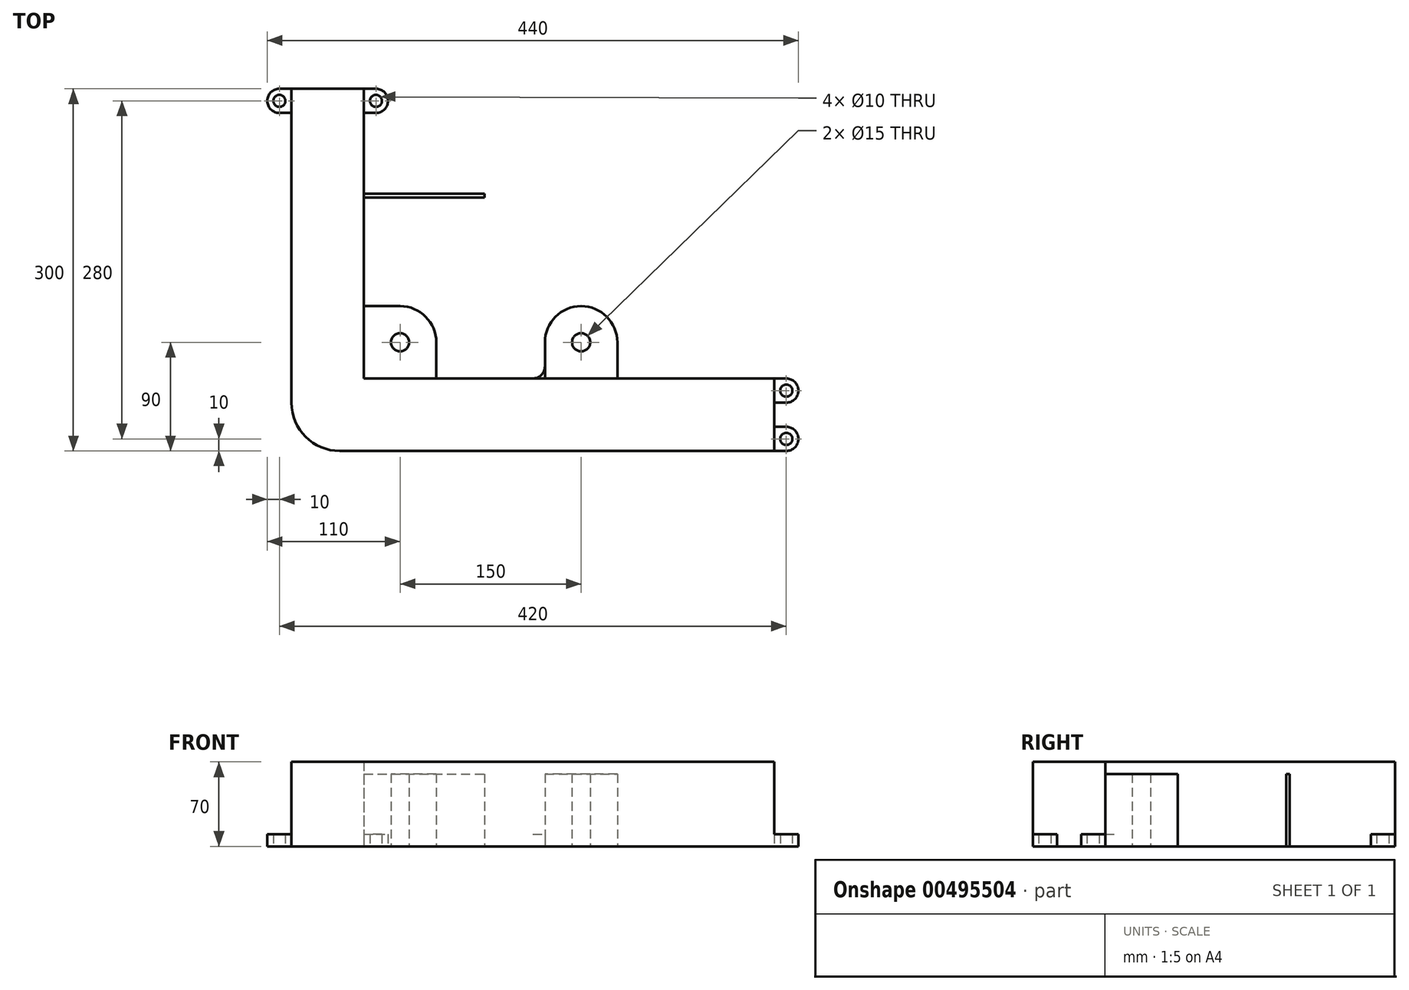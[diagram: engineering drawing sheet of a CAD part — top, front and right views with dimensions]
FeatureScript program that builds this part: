
annotation { "Feature Type Name" : "Feature", "Feature Type Description" : "" }
export const myFeature = defineFeature(function(context is Context, id is Id, definition is map)
    precondition{}
    {
        {
            var Q0;
            Q0=qCreatedBy(makeId("Top.planeOp"),FACE);
            var sketch = newSketch(context, id + "F0", { "sketchPlane" : qUnion([Q0])});
            skLineSegment(sketch, "E0", {"start": v(0, 40) * mm, "end": v(0, 300) * mm});
            skLineSegment(sketch, "E1", {"start": v(400, 60) * mm, "end": v(400, 0) * mm});
            skLineSegment(sketch, "E2", {"start": v(40, 0) * mm, "end": v(400, 0) * mm});
            skLineSegment(sketch, "E3", {"start": v(60, 300) * mm, "end": v(0, 300) * mm});
            skLineSegment(sketch, "E4.top", {"start": v(60, 120) * mm, "end": v(90, 120) * mm});
            skLineSegment(sketch, "E4.right", {"start": v(120, 60) * mm, "end": v(120, 90) * mm});
            skCircle(sketch, "E5", {"center": v(90, 90) * mm, "radius": 7.5 * mm});
            skLineSegment(sketch, "E6", {"start": v(60, 120) * mm, "end": v(60, 300) * mm});
            skLineSegment(sketch, "E7", {"start": v(120, 60) * mm, "end": v(400, 60) * mm});
            skLineSegment(sketch, "E8", {"start": v(60, 120) * mm, "end": v(60, 60) * mm});
            skLineSegment(sketch, "E9", {"start": v(60, 60) * mm, "end": v(120, 60) * mm});
            skLineSegment(sketch, "E10", {"start": v(0, 300) * mm, "end": v(-10, 300) * mm});
            skLineSegment(sketch, "E11", {"start": v(-10, 280) * mm, "end": v(0, 280) * mm});
            skLineSegment(sketch, "E12", {"start": v(60, 300) * mm, "end": v(70, 300) * mm});
            skLineSegment(sketch, "E13", {"start": v(70, 280) * mm, "end": v(60, 280) * mm});
            skLineSegment(sketch, "E14", {"start": v(210, 60) * mm, "end": v(210, 90) * mm});
            skLineSegment(sketch, "E15", {"start": v(270, 90) * mm, "end": v(270, 60) * mm});
            skPoint(sketch, "E16.visualSharp", {"position": v(120, 120) * mm});
            skArc(sketch, "E16.filletArc", {"start": v(120, 90) * mm, "mid": v(111.21, 111.21) * mm, "end": v(90, 120) * mm});
            skLineSegment(sketch, "E17", {"start": v(-10, 300) * mm, "end": v(-10, 280) * mm, "construction": true});
            skLineSegment(sketch, "E18", {"start": v(70, 300) * mm, "end": v(70, 280) * mm, "construction": true});
            skArc(sketch, "E19", {"start": v(-10, 300) * mm, "mid": v(-20, 290) * mm, "end": v(-10, 280) * mm});
            skArc(sketch, "E20", {"start": v(70, 280) * mm, "mid": v(80, 290) * mm, "end": v(70, 300) * mm});
            skCircle(sketch, "E21", {"center": v(-10, 290) * mm, "radius": 5 * mm});
            skArc(sketch, "E22", {"start": v(270, 90) * mm, "mid": v(240, 120) * mm, "end": v(210, 90) * mm});
            skLineSegment(sketch, "E23", {"start": v(210, 90) * mm, "end": v(270, 90) * mm, "construction": true});
            skPoint(sketch, "E24.visualSharp", {"position": v(0, 0) * mm});
            skArc(sketch, "E24.filletArc", {"start": v(0, 40) * mm, "mid": v(11.72, 11.72) * mm, "end": v(40, 0) * mm});
            skLineSegment(sketch, "E25", {"start": v(400, 60) * mm, "end": v(410, 60) * mm});
            skLineSegment(sketch, "E26", {"start": v(410, 60) * mm, "end": v(410, 40) * mm, "construction": true});
            skLineSegment(sketch, "E27", {"start": v(410, 40) * mm, "end": v(400, 40) * mm});
            skLineSegment(sketch, "E28", {"start": v(400, 20) * mm, "end": v(410, 20) * mm});
            skLineSegment(sketch, "E29", {"start": v(410, 20) * mm, "end": v(410, 0) * mm, "construction": true});
            skLineSegment(sketch, "E30", {"start": v(410, 0) * mm, "end": v(400, 0) * mm});
            skCircle(sketch, "E31", {"center": v(70, 290) * mm, "radius": 5 * mm});
            skArc(sketch, "E32", {"start": v(410, 40) * mm, "mid": v(420, 50) * mm, "end": v(410, 60) * mm});
            skArc(sketch, "E33", {"start": v(410, 0) * mm, "mid": v(420, 10) * mm, "end": v(410, 20) * mm});
            skArc(sketch, "E34", {"start": v(200, 60) * mm, "mid": v(207.07, 62.93) * mm, "end": v(210, 70) * mm});
            skCircle(sketch, "E35", {"center": v(410, 50) * mm, "radius": 5 * mm});
            skCircle(sketch, "E36", {"center": v(410, 10) * mm, "radius": 5 * mm});
            skLineSegment(sketch, "E37.bottom", {"start": v(60, 210) * mm, "end": v(160, 210) * mm});
            skLineSegment(sketch, "E37.top", {"start": v(60, 213) * mm, "end": v(160, 213) * mm});
            skLineSegment(sketch, "E37.left", {"start": v(60, 210) * mm, "end": v(60, 213) * mm});
            skLineSegment(sketch, "E37.right", {"start": v(160, 210) * mm, "end": v(160, 213) * mm});
            skCircle(sketch, "E38", {"center": v(240, 90) * mm, "radius": 7.5 * mm});
            skLineSegment(sketch, "E39.bottom", {"start": v(330, 60) * mm, "end": v(380, 60) * mm});
            skLineSegment(sketch, "E39.top", {"start": v(330, 110) * mm, "end": v(380, 110) * mm});
            skLineSegment(sketch, "E39.left", {"start": v(330, 60) * mm, "end": v(330, 110) * mm});
            skLineSegment(sketch, "E39.right", {"start": v(380, 60) * mm, "end": v(380, 110) * mm});
            skSolve(sketch);
        }
        {
            var Q0;
            {var subQ4=sQuery(id+"F0.wireOp",EDGE,"E2");Q0=makeQuery(id+"F0.imprint","IMPRINT",FACE,{"disambiguationData":[TD([[makeQuery(id+"F0.imprint","IMPRINT",EDGE,{"derivedFrom":subQ4}),1.0]])]});}
            extrude(context, id + "F1", {"entities" : qUnion([Q0]), "depth" : 70 * mm});
        }
        {
            var Q0;
            Q0=makeQuery(id+"F0.imprint","IMPRINT",FACE,{"disambiguationData":[TD([[makeQuery(id+"F0.imprint","IMPRINT",EDGE,{"derivedFrom":sQuery(id+"F0.wireOp",EDGE,"E4.top")}),-1.0]])]});
            var Q1;
            {var subQ5=sQuery(id+"F0.wireOp",EDGE,"E15");Q1=makeQuery(id+"F0.imprint","IMPRINT",FACE,{"disambiguationData":[TD([[makeQuery(id+"F0.imprint","IMPRINT",EDGE,{"derivedFrom":subQ5}),-1.0]])]});}
            var Q2;
            Q2=makeQuery(id+"F0.imprint","IMPRINT",FACE,{"disambiguationData":[TD([[makeQuery(id+"F0.imprint","IMPRINT",EDGE,{"derivedFrom":sQuery(id+"F0.wireOp",EDGE,"E37.bottom")}),1.0]])]});
            var Q3;
            Q3=makeQuery(id+"F0.imprint","IMPRINT",FACE,{"disambiguationData":[TD([[makeQuery(id+"F0.imprint","IMPRINT",EDGE,{"derivedFrom":sQuery(id+"F0.wireOp",EDGE,"E39.bottom")}),1.0]])]});
            extrude(context, id + "F2", {"entities" : qUnion([Q0, Q1, Q2, Q3]), "operationType" : NewBodyOperationType.ADD, "depth" : 60 * mm});
        }
        {
            var Q0;
            {var subQ3=sQuery(id+"F0.wireOp",EDGE,"E34");Q0=makeQuery(id+"F0.imprint","IMPRINT",FACE,{"disambiguationData":[TD([[makeQuery(id+"F0.imprint","IMPRINT",EDGE,{"derivedFrom":subQ3}),-1.0]])]});}
            var Q1;
            {var subQ1=sQuery(id+"F0.wireOp",EDGE,"E25");Q1=makeQuery(id+"F0.imprint","IMPRINT",FACE,{"disambiguationData":[TD([[makeQuery(id+"F0.imprint","IMPRINT",EDGE,{"derivedFrom":subQ1}),-1.0]])]});}
            var Q2;
            {var subQ1=sQuery(id+"F0.wireOp",EDGE,"E28");Q2=makeQuery(id+"F0.imprint","IMPRINT",FACE,{"disambiguationData":[TD([[makeQuery(id+"F0.imprint","IMPRINT",EDGE,{"derivedFrom":subQ1}),-1.0]])]});}
            var Q3;
            {var subQ0=sQuery(id+"F0.wireOp",EDGE,"E12");Q3=makeQuery(id+"F0.imprint","IMPRINT",FACE,{"disambiguationData":[TD([[makeQuery(id+"F0.imprint","IMPRINT",EDGE,{"derivedFrom":subQ0}),-1.0]])]});}
            var Q4;
            {var subQ1=sQuery(id+"F0.wireOp",EDGE,"E10");Q4=makeQuery(id+"F0.imprint","IMPRINT",FACE,{"disambiguationData":[TD([[makeQuery(id+"F0.imprint","IMPRINT",EDGE,{"derivedFrom":subQ1}),1.0]])]});}
            extrude(context, id + "F3", {"entities" : qUnion([Q0, Q1, Q2, Q3, Q4]), "operationType" : NewBodyOperationType.ADD, "depth" : 10 * mm});
        }
    });
